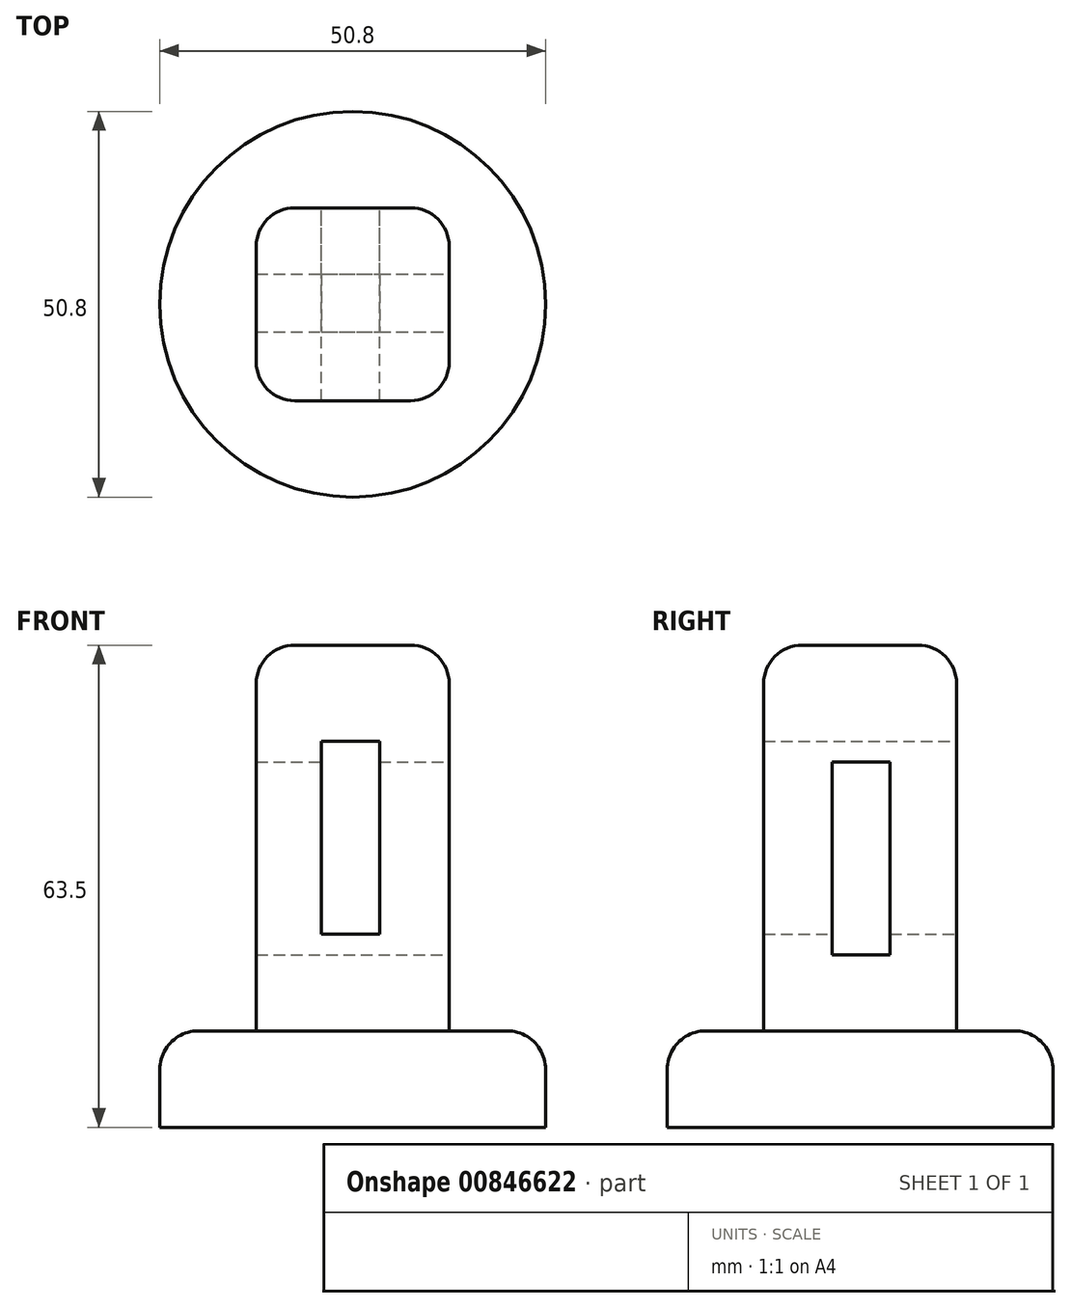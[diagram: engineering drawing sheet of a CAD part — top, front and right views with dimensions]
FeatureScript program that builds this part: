
annotation { "Feature Type Name" : "Feature", "Feature Type Description" : "" }
export const myFeature = defineFeature(function(context is Context, id is Id, definition is map)
    precondition{}
    {
        {
            var Q0;
            Q0=qCreatedBy(makeId("Top.planeOp"),FACE);
            var sketch = newSketch(context, id + "F0", { "sketchPlane" : qUnion([Q0])});
            skCircle(sketch, "E0", {"center": v(0, 0) * mm, "radius": 25.4 * mm});
            skSolve(sketch);
        }
        {
            var Q0;
            Q0 = qSketchRegion(id + "F0", true);
            extrude(context, id + "F1", {"entities" : qUnion([Q0]), "depth" : 12.7 * mm, "offsetDistance" : 25.4 * mm});
        }
        {
            var Q0;
            Q0=makeQuery(id+"F1.opExtrude","CAP_FACE",FACE,{"disambiguationData":[OSD([sQuery(id+"F0.wireOp",EDGE,"E0")])],"isStart":false});
            var sketch = newSketch(context, id + "F2", { "sketchPlane" : qUnion([Q0])});
            skLineSegment(sketch, "E1.bottom", {"start": v(-12.7, 12.7) * mm, "end": v(12.7, 12.7) * mm});
            skLineSegment(sketch, "E1.top", {"start": v(-12.7, -12.7) * mm, "end": v(12.7, -12.7) * mm});
            skLineSegment(sketch, "E1.left", {"start": v(-12.7, 12.7) * mm, "end": v(-12.7, -12.7) * mm});
            skLineSegment(sketch, "E1.right", {"start": v(12.7, 12.7) * mm, "end": v(12.7, -12.7) * mm});
            skPoint(sketch, "E1.middle", {"position": v(0, 0) * mm});
            skSolve(sketch);
        }
        {
            var Q0;
            Q0 = qSketchRegion(id + "F2", true);
            extrude(context, id + "F3", {"entities" : qUnion([Q0]), "operationType" : NewBodyOperationType.ADD, "depth" : 50.8 * mm, "offsetDistance" : 25.4 * mm});
        }
        {
            var Q0;
            Q0=makeQuery(id+"F3.opExtrude","SWEPT_EDGE",EDGE,{"disambiguationData":[OSD([sQuery(id+"F2.wireOp",EDGE,"E1.top"),sQuery(id+"F2.wireOp",EDGE,"E1.right")])]});
            var Q1;
            Q1=makeQuery(id+"F3.opExtrude","SWEPT_EDGE",EDGE,{"disambiguationData":[OSD([sQuery(id+"F2.wireOp",EDGE,"E1.top"),sQuery(id+"F2.wireOp",EDGE,"E1.left")])]});
            var Q2;
            Q2=makeQuery(id+"F3.opExtrude","SWEPT_EDGE",EDGE,{"disambiguationData":[OSD([sQuery(id+"F2.wireOp",EDGE,"E1.bottom"),sQuery(id+"F2.wireOp",EDGE,"E1.right")])]});
            var Q3;
            Q3=makeQuery(id+"F3.opExtrude","SWEPT_EDGE",EDGE,{"disambiguationData":[OSD([sQuery(id+"F2.wireOp",EDGE,"E1.bottom"),sQuery(id+"F2.wireOp",EDGE,"E1.left")])]});
            var Q4;
            Q4=makeQuery(id+"F1.opExtrude","CAP_EDGE",EDGE,{"disambiguationData":[OSD([sQuery(id+"F0.wireOp",EDGE,"E0")])],"isStart":false});
            var Q5;
            Q5=makeQuery(id+"F3.opExtrude","CAP_EDGE",EDGE,{"disambiguationData":[OSD([sQuery(id+"F2.wireOp",EDGE,"E1.left")])],"isStart":false});
            var Q6;
            Q6=makeQuery(id+"F3.opExtrude","CAP_EDGE",EDGE,{"disambiguationData":[OSD([sQuery(id+"F2.wireOp",EDGE,"E1.top")])],"isStart":false});
            var Q7;
            Q7=makeQuery(id+"F3.opExtrude","CAP_EDGE",EDGE,{"disambiguationData":[OSD([sQuery(id+"F2.wireOp",EDGE,"E1.right")])],"isStart":false});
            var Q8;
            Q8=makeQuery(id+"F3.opExtrude","CAP_EDGE",EDGE,{"disambiguationData":[OSD([sQuery(id+"F2.wireOp",EDGE,"E1.bottom")])],"isStart":false});
            fillet(context, id + "F4", {"entities" : qUnion([Q0, Q1, Q2, Q3, Q4, Q5, Q6, Q7, Q8]), "radius" : 5.08 * mm, "tangentPropagation" : true, "allowEdgeOverflow" : false});
        }
        {
            var Q0;
            Q0=makeQuery(id+"F3.opExtrude","SWEPT_FACE",FACE,{"disambiguationData":[OSD([sQuery(id+"F2.wireOp",EDGE,"E1.right")])]});
            var sketch = newSketch(context, id + "F5", { "sketchPlane" : qUnion([Q0])});
            skLineSegment(sketch, "E2.bottom", {"start": v(-3.67, 48.14) * mm, "end": v(3.95, 48.14) * mm});
            skLineSegment(sketch, "E2.top", {"start": v(-3.67, 22.74) * mm, "end": v(3.95, 22.74) * mm});
            skLineSegment(sketch, "E2.left", {"start": v(-3.67, 48.14) * mm, "end": v(-3.67, 22.74) * mm});
            skLineSegment(sketch, "E2.right", {"start": v(3.95, 48.14) * mm, "end": v(3.95, 22.74) * mm});
            skSolve(sketch);
        }
        {
            var Q0;
            Q0=makeQuery(id+"F5.imprint","IMPRINT",FACE,{"disambiguationData":[TD([[makeQuery(id+"F5.imprint","IMPRINT",EDGE,{"derivedFrom":sQuery(id+"F5.wireOp",EDGE,"E2.bottom")}),-1.0]])]});
            extrude(context, id + "F6", {"entities" : qUnion([Q0]), "operationType" : NewBodyOperationType.REMOVE, "oppositeDirection" : true, "depth" : 25.4 * mm, "offsetDistance" : 25.4 * mm});
        }
        {
            var Q0;
            Q0=makeQuery(id+"F3.opExtrude","SWEPT_FACE",FACE,{"disambiguationData":[OSD([sQuery(id+"F2.wireOp",EDGE,"E1.bottom")])]});
            var sketch = newSketch(context, id + "F7", { "sketchPlane" : qUnion([Q0])});
            skLineSegment(sketch, "E3.bottom", {"start": v(-3.52, 50.85) * mm, "end": v(4.1, 50.85) * mm});
            skLineSegment(sketch, "E3.top", {"start": v(-3.52, 25.45) * mm, "end": v(4.1, 25.45) * mm});
            skLineSegment(sketch, "E3.left", {"start": v(-3.52, 50.85) * mm, "end": v(-3.52, 25.45) * mm});
            skLineSegment(sketch, "E3.right", {"start": v(4.1, 50.85) * mm, "end": v(4.1, 25.45) * mm});
            skSolve(sketch);
        }
        {
            var Q0;
            Q0=makeQuery(id+"F7.imprint","IMPRINT",FACE,{"disambiguationData":[TD([[makeQuery(id+"F7.imprint","IMPRINT",EDGE,{"derivedFrom":sQuery(id+"F7.wireOp",EDGE,"E3.bottom")}),-1.0]])]});
            extrude(context, id + "F8", {"entities" : qUnion([Q0]), "operationType" : NewBodyOperationType.REMOVE, "oppositeDirection" : true, "depth" : 25.4 * mm, "offsetDistance" : 25.4 * mm});
        }
    });
